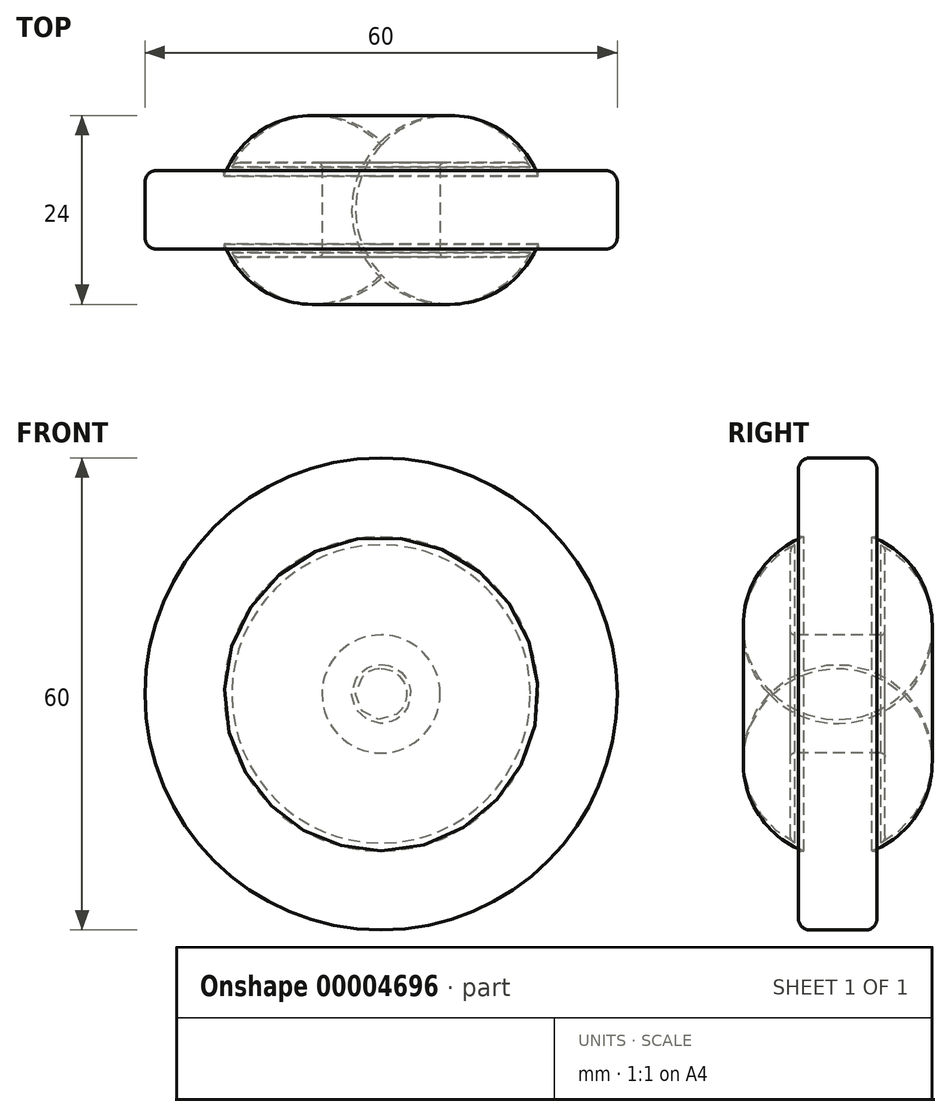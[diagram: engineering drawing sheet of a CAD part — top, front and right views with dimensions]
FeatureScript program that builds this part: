
annotation { "Feature Type Name" : "Feature", "Feature Type Description" : "" }
export const myFeature = defineFeature(function(context is Context, id is Id, definition is map)
    precondition{}
    {
        {
            var Q0;
            Q0=qCreatedBy(makeId("Right.planeOp"),FACE);
            var sketch = newSketch(context, id + "F0", { "sketchPlane" : qUnion([Q0])});
            skLineSegment(sketch, "E0", {"start": v(0, 0) * mm, "end": v(12, 0) * mm, "construction": true});
            skLineSegment(sketch, "E1", {"start": v(0.5, 7.5) * mm, "end": v(11.5, 7.5) * mm});
            skLineSegment(sketch, "E2", {"start": v(12, 8) * mm, "end": v(12, 18.06) * mm});
            skLineSegment(sketch, "E3", {"start": v(0, 8) * mm, "end": v(0, 18.06) * mm});
            skLineSegment(sketch, "E4", {"start": v(0, 18.65) * mm, "end": v(12, 18.65) * mm, "construction": true});
            skArc(sketch, "E5", {"start": v(11.45, 18.95) * mm, "mid": v(6, 20.26) * mm, "end": v(0.55, 18.95) * mm});
            skLineSegment(sketch, "E6", {"start": v(1, 20.42) * mm, "end": v(1, 28.5) * mm});
            skLineSegment(sketch, "E7", {"start": v(2.5, 30) * mm, "end": v(9.5, 30) * mm});
            skLineSegment(sketch, "E8", {"start": v(11, 28.5) * mm, "end": v(11, 20.42) * mm});
            skArc(sketch, "E9", {"start": v(10.32, 19.96) * mm, "mid": v(6, 20.76) * mm, "end": v(1.68, 19.96) * mm});
            skPoint(sketch, "E10.visualSharp", {"position": v(0, 18.65) * mm});
            skArc(sketch, "E10.filletArc", {"start": v(0.55, 18.95) * mm, "mid": v(0.15, 18.58) * mm, "end": v(0, 18.06) * mm});
            skPoint(sketch, "E11.visualSharp", {"position": v(12, 18.65) * mm});
            skArc(sketch, "E11.filletArc", {"start": v(12, 18.06) * mm, "mid": v(11.85, 18.58) * mm, "end": v(11.45, 18.95) * mm});
            skPoint(sketch, "E12.visualSharp", {"position": v(1, 30) * mm});
            skArc(sketch, "E12.filletArc", {"start": v(2.5, 30) * mm, "mid": v(1.44, 29.56) * mm, "end": v(1, 28.5) * mm});
            skPoint(sketch, "E13.visualSharp", {"position": v(11, 30) * mm});
            skArc(sketch, "E13.filletArc", {"start": v(11, 28.5) * mm, "mid": v(10.56, 29.56) * mm, "end": v(9.5, 30) * mm});
            skPoint(sketch, "E14.visualSharp", {"position": v(1, 19.67) * mm});
            skArc(sketch, "E14.filletArc", {"start": v(1, 20.42) * mm, "mid": v(1.22, 20.01) * mm, "end": v(1.68, 19.96) * mm});
            skPoint(sketch, "E15.visualSharp", {"position": v(11, 19.67) * mm});
            skArc(sketch, "E15.filletArc", {"start": v(10.32, 19.96) * mm, "mid": v(10.78, 20.01) * mm, "end": v(11, 20.42) * mm});
            skPoint(sketch, "E16.visualSharp", {"position": v(0, 7.5) * mm});
            skArc(sketch, "E16.filletArc", {"start": v(0, 8) * mm, "mid": v(0.15, 7.65) * mm, "end": v(0.5, 7.5) * mm});
            skPoint(sketch, "E17.visualSharp", {"position": v(12, 7.5) * mm});
            skArc(sketch, "E17.filletArc", {"start": v(11.5, 7.5) * mm, "mid": v(11.85, 7.65) * mm, "end": v(12, 8) * mm});
            skSolve(sketch);
        }
        {
            var Q0;
            Q0 = qSketchRegion(id + "F0", true);
            var Q1;
            Q1=sQuery(id+"F0.wireOp",EDGE,"E0");
            revolve(context, id + "F1", {"entities" : qUnion([Q0]), "axis" : qUnion([Q1]), "revolveType" : RevolveType.FULL});
        }
    });
